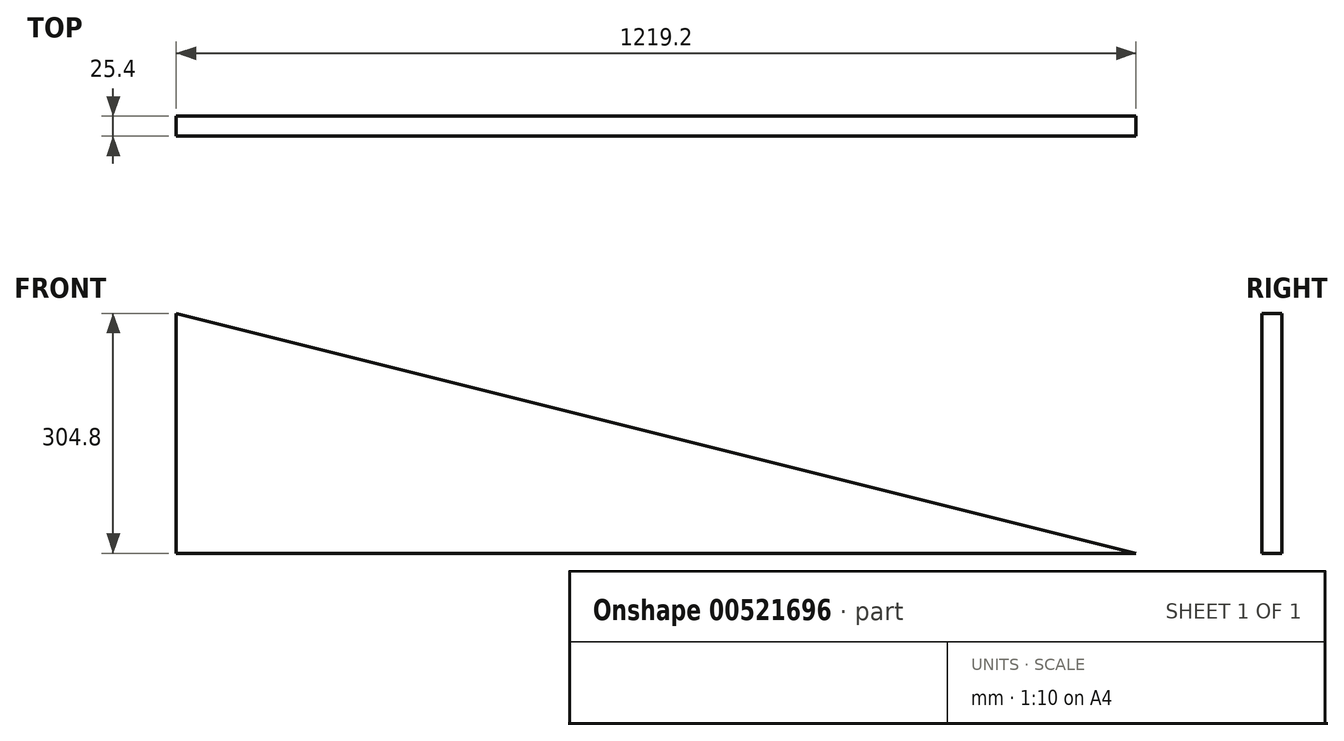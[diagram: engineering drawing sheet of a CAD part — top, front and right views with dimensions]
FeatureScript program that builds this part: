
annotation { "Feature Type Name" : "Feature", "Feature Type Description" : "" }
export const myFeature = defineFeature(function(context is Context, id is Id, definition is map)
    precondition{}
    {
        {
            var Q0;
            Q0=qCreatedBy(makeId("Front.planeOp"),FACE);
            var sketch = newSketch(context, id + "F0", { "sketchPlane" : qUnion([Q0])});
            skLineSegment(sketch, "E0", {"start": v(0, 0) * mm, "end": v(0, 304.8) * mm});
            skLineSegment(sketch, "E1", {"start": v(0, 304.8) * mm, "end": v(1219.2, 0) * mm});
            skLineSegment(sketch, "E2", {"start": v(1219.2, 0) * mm, "end": v(0, 0) * mm});
            skSolve(sketch);
        }
        {
            var Q0;
            Q0 = qSketchRegion(id + "F0", true);
            extrude(context, id + "F1", {"entities" : qUnion([Q0]), "depth" : 25.4 * mm, "offsetDistance" : 25.4 * mm});
        }
    });
